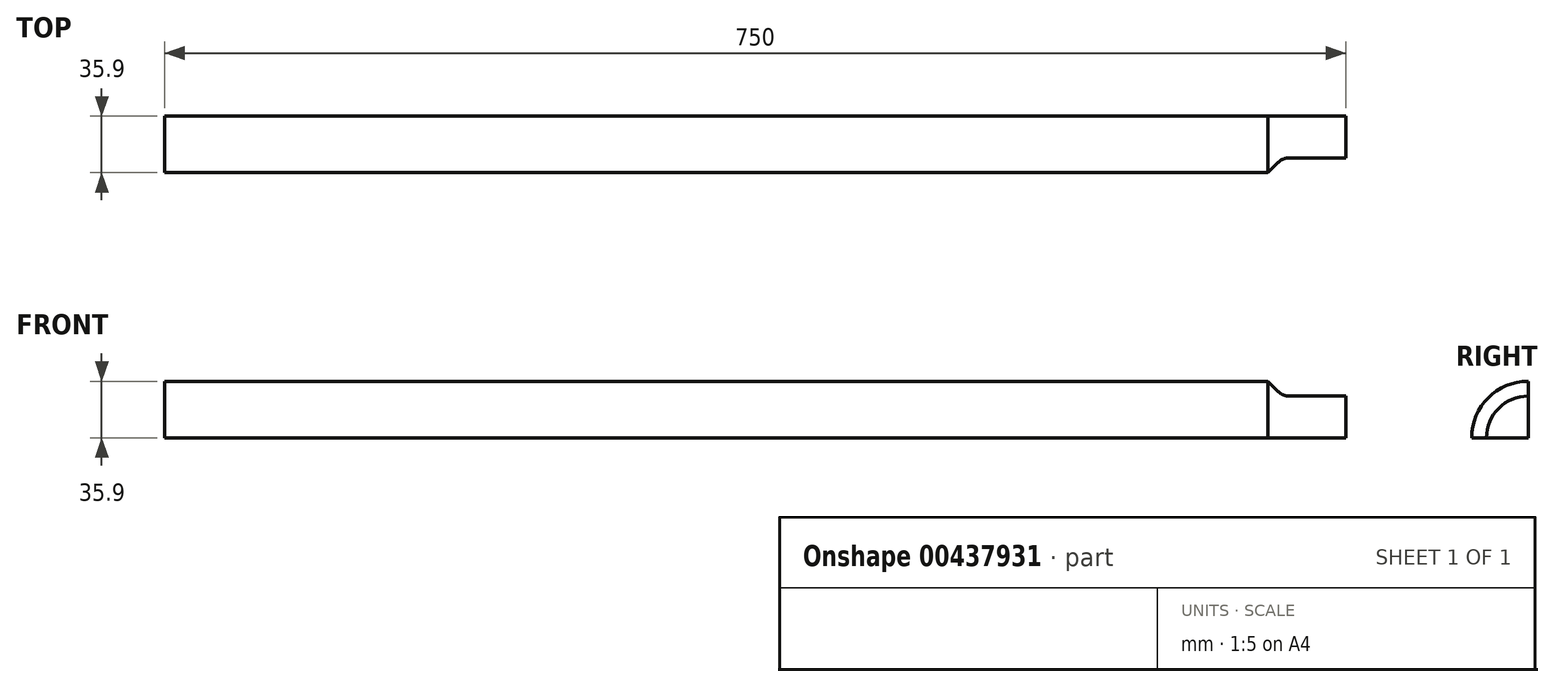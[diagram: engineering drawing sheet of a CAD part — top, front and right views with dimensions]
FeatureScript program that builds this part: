
annotation { "Feature Type Name" : "Feature", "Feature Type Description" : "" }
export const myFeature = defineFeature(function(context is Context, id is Id, definition is map)
    precondition{}
    {
        {
            var Q0;
            Q0=qCreatedBy(makeId("Front.planeOp"),FACE);
            var sketch = newSketch(context, id + "F0", { "sketchPlane" : qUnion([Q0])});
            skLineSegment(sketch, "E0.bottom", {"start": v(0, 35.9) * mm, "end": v(700.6, 35.9) * mm});
            skLineSegment(sketch, "E0.top", {"start": v(0, 0) * mm, "end": v(750, 0) * mm});
            skLineSegment(sketch, "E0.left", {"start": v(0, 35.9) * mm, "end": v(0, 0) * mm});
            skLineSegment(sketch, "E1.bottom", {"start": v(0, 24.08) * mm, "end": v(0, 24.08) * mm});
            skLineSegment(sketch, "E1.top", {"start": v(0, 35.9) * mm, "end": v(0, 35.9) * mm});
            skLineSegment(sketch, "E1.left", {"start": v(0, 35.9) * mm, "end": v(0, 24.08) * mm});
            skLineSegment(sketch, "E1.right", {"start": v(0, 35.9) * mm, "end": v(0, 24.08) * mm});
            skLineSegment(sketch, "E2", {"start": v(710, 26.5) * mm, "end": v(750, 26.5) * mm});
            skLineSegment(sketch, "E3", {"start": v(750, 26.5) * mm, "end": v(750, 0) * mm});
            skLineSegment(sketch, "E4", {"start": v(710, 26.5) * mm, "end": v(700.6, 35.9) * mm});
            skPoint(sketch, "E5.end.orphan", {"position": v(750, 26.5) * mm});
            skSolve(sketch);
        }
        {
            var Q0;
            Q0=makeQuery(id+"F0.imprint","IMPRINT",FACE,{"disambiguationData":[TD([[makeQuery(id+"F0.imprint","IMPRINT",EDGE,{"derivedFrom":sQuery(id+"F0.wireOp",EDGE,"E0.bottom")}),-1.0]])]});
            var Q1;
            Q1=sQuery(id+"F0.wireOp",EDGE,"E0.bottom");
            var Q2;
            Q2=sQuery(id+"F0.wireOp",EDGE,"E0.top");
            var Q3;
            Q3=sQuery(id+"F0.wireOp",EDGE,"E0.top");
            revolve(context, id + "F1", {"entities" : qUnion([Q0]), "surfaceEntities" : qUnion([Q1, Q2]), "axis" : qUnion([Q3]), "revolveType" : RevolveType.ONE_DIRECTION, "angle" : 90 * degree});
        }
        {
            var Q0;
            Q0=makeQuery(id+"F1.opRevolve","SWEPT_EDGE",EDGE,{"disambiguationData":[OSD([sQuery(id+"F0.wireOp",EDGE,"E2"),sQuery(id+"F0.wireOp",EDGE,"E4")])]});
            fillet(context, id + "F2", {"entities" : qUnion([Q0]), "radius" : 10 * mm, "tangentPropagation" : true, "allowEdgeOverflow" : false});
        }
    });
